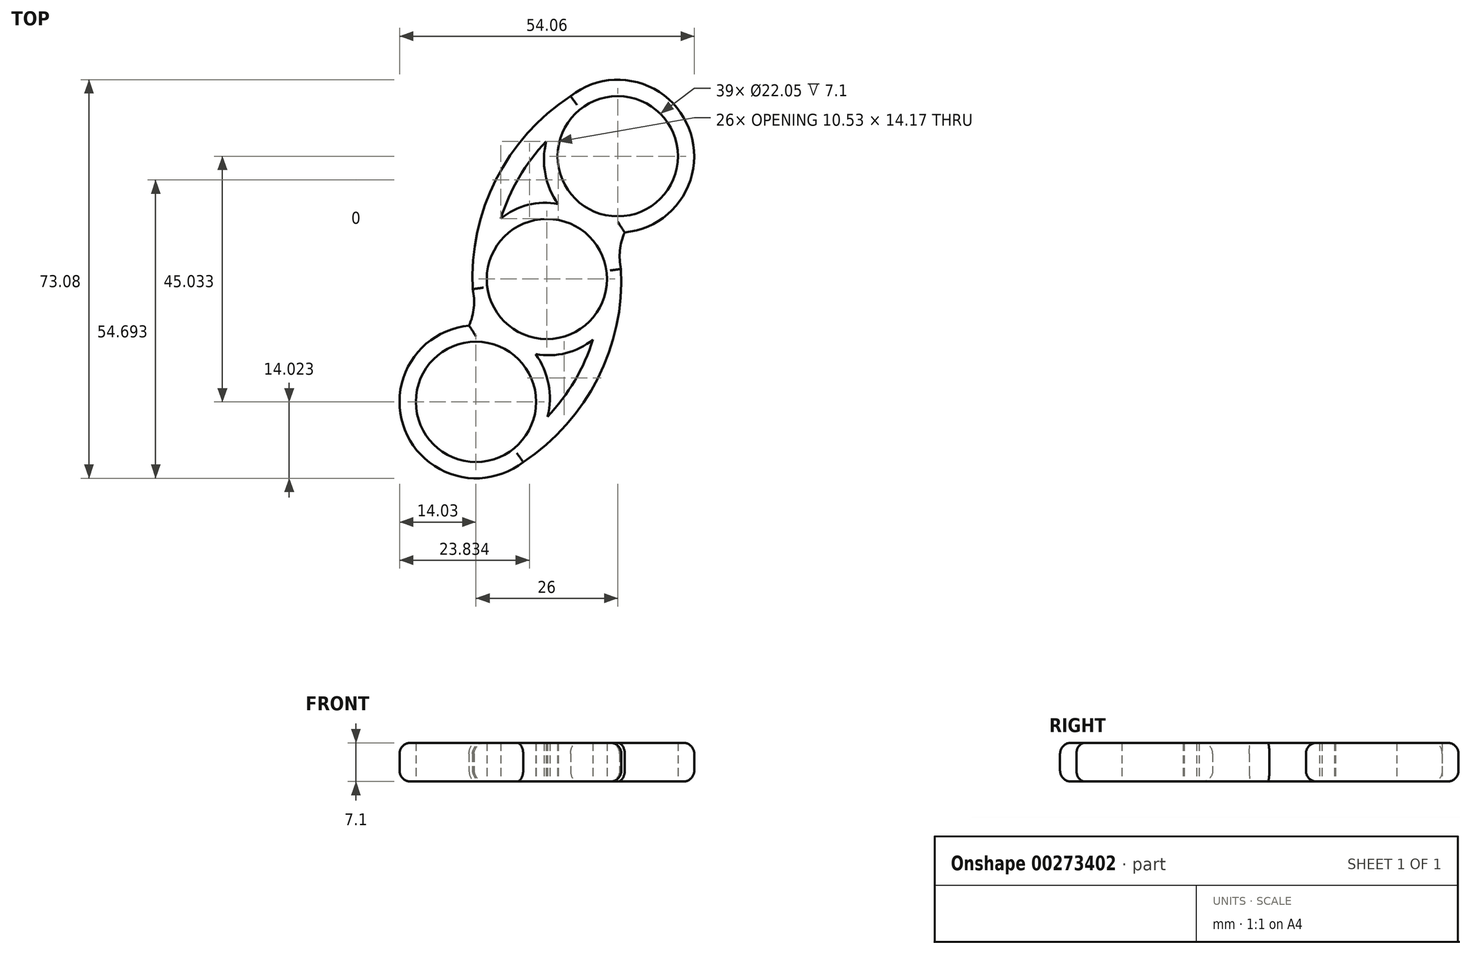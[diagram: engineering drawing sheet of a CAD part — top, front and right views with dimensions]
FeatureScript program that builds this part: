
annotation { "Feature Type Name" : "Feature", "Feature Type Description" : "" }
export const myFeature = defineFeature(function(context is Context, id is Id, definition is map)
    precondition{}
    {
        {
            var Q0;
            Q0=qCreatedBy(makeId("Top.planeOp"),FACE);
            var sketch = newSketch(context, id + "F0", { "sketchPlane" : qUnion([Q0])});
            skCircle(sketch, "E0", {"center": v(0, 0) * mm, "radius": 11.03 * mm});
            skCircle(sketch, "E1", {"center": v(13, 22.52) * mm, "radius": 11.03 * mm});
            skLineSegment(sketch, "E2", {"start": v(0, 0) * mm, "end": v(13, 22.52) * mm, "construction": true});
            skArc(sketch, "E3", {"start": v(14.28, 8.55) * mm, "mid": v(26.03, 27.7) * mm, "end": v(4.35, 33.55) * mm});
            skLineSegment(sketch, "E4", {"start": v(13, 22.52) * mm, "end": v(0.85, 29.53) * mm, "construction": true});
            skPoint(sketch, "E5.visualSharp", {"position": v(5.99, 10.37) * mm});
            skLineSegment(sketch, "E6", {"start": v(13, 22.52) * mm, "end": v(25.15, 15.5) * mm, "construction": true});
            skCircle(sketch, "E7", {"center": v(0, 0) * mm, "radius": 11.36 * mm, "construction": true});
            skPoint(sketch, "E8.center", {"position": v(-0.23, 0.06) * mm});
            skPoint(sketch, "E9.orphan", {"position": v(-5.27, 14.87) * mm});
            skPoint(sketch, "E10.orphan", {"position": v(7.2, 12.48) * mm});
            skPoint(sketch, "E11.1.5", {"position": v(0.06, -0.23) * mm});
            skPoint(sketch, "E11.1.6", {"position": v(-10.25, -11) * mm});
            skPoint(sketch, "E11.2.5", {"position": v(0.17, 0.17) * mm});
            skCircle(sketch, "E12.1.0", {"center": v(-13, -22.52) * mm, "radius": 11.03 * mm});
            skLineSegment(sketch, "E12.1.1", {"start": v(-13, -22.52) * mm, "end": v(-0.85, -29.53) * mm, "construction": true});
            skArc(sketch, "E12.1.2", {"start": v(-14.28, -8.55) * mm, "mid": v(-26.03, -27.7) * mm, "end": v(-4.35, -33.55) * mm});
            skLineSegment(sketch, "E12.1.3", {"start": v(-13, -22.52) * mm, "end": v(-25.15, -15.5) * mm, "construction": true});
            skArc(sketch, "E13", {"start": v(-4.35, -33.55) * mm, "mid": v(9.34, -18.24) * mm, "end": v(13.6, 1.84) * mm});
            skArc(sketch, "E14", {"start": v(14.28, 8.55) * mm, "mid": v(13.4, 5.25) * mm, "end": v(13.6, 1.84) * mm});
            skArc(sketch, "E15.1.0", {"start": v(-14.28, -8.55) * mm, "mid": v(-13.4, -5.25) * mm, "end": v(-13.6, -1.84) * mm});
            skArc(sketch, "E15.1.1", {"start": v(4.35, 33.55) * mm, "mid": v(-9.34, 18.24) * mm, "end": v(-13.6, -1.84) * mm});
            skArc(sketch, "E16", {"start": v(2.07, 13.75) * mm, "mid": v(-3.5, 13.58) * mm, "end": v(-8.46, 11.07) * mm});
            skArc(sketch, "E17", {"start": v(-0.13, 25.24) * mm, "mid": v(-0.3, 19.25) * mm, "end": v(2.07, 13.75) * mm});
            skPoint(sketch, "E18.orphan", {"position": v(1.15, 27.06) * mm});
            skPoint(sketch, "E19.orphan", {"position": v(3.03, 13.53) * mm});
            skArc(sketch, "E20.0", {"start": v(-0.13, 25.24) * mm, "mid": v(-5.1, 18.63) * mm, "end": v(-8.46, 11.07) * mm});
            skPoint(sketch, "E21.orphan", {"position": v(-9.03, 10.57) * mm});
            skPoint(sketch, "E22.orphan", {"position": v(0.1, 26.05) * mm});
            skArc(sketch, "E23.1.0", {"start": v(0.13, -25.24) * mm, "mid": v(5.1, -18.63) * mm, "end": v(8.46, -11.07) * mm});
            skArc(sketch, "E23.1.1", {"start": v(0.13, -25.24) * mm, "mid": v(0.3, -19.25) * mm, "end": v(-2.07, -13.75) * mm});
            skArc(sketch, "E23.1.2", {"start": v(-2.07, -13.75) * mm, "mid": v(3.5, -13.58) * mm, "end": v(8.46, -11.07) * mm});
            skSolve(sketch);
        }
        {
            var Q0;
            Q0=makeQuery(id+"F0.imprint","IMPRINT",FACE,{"disambiguationData":[TD([[makeQuery(id+"F0.imprint","IMPRINT",EDGE,{"derivedFrom":sQuery(id+"F0.wireOp",EDGE,"ea44153e-c5e4-4200-878d-53ebf284e07f.1.0")}),-1.0]])]});
            var Q1;
            Q1=makeQuery(id+"F0.imprint","IMPRINT",FACE,{"disambiguationData":[TD([[makeQuery(id+"F0.imprint","IMPRINT",EDGE,{"derivedFrom":sQuery(id+"F0.wireOp",EDGE,"E0")}),-1.0]])]});
            var Q2;
            Q2=makeQuery(id+"F0.imprint","IMPRINT",FACE,{"disambiguationData":[TD([[makeQuery(id+"F0.imprint","IMPRINT",EDGE,{"derivedFrom":sQuery(id+"F0.wireOp",EDGE,"E1")}),-1.0]])]});
            var Q3;
            {var subQ0=sQuery(id+"F0.wireOp",EDGE,"zqQpl2xC-KShR-byGl-JfGq-b1LpVGurQPJH");Q3=makeQuery(id+"F0.imprint","IMPRINT",FACE,{"disambiguationData":[TD([[makeQuery(id+"F0.imprint","IMPRINT",EDGE,{"derivedFrom":subQ0}),-1.0]])]});}
            extrude(context, id + "F1", {"entities" : qUnion([Q0, Q1, Q2, Q3]), "depth" : 7.1 * mm});
        }
        {
            var Q0;
            Q0=makeQuery(id+"F1.opExtrude","CAP_EDGE",EDGE,{"disambiguationData":[OSD([sQuery(id+"F0.wireOp",EDGE,"E15.1.1")])],"isStart":false});
            var Q1;
            Q1=makeQuery(id+"F1.opExtrude","CAP_EDGE",EDGE,{"disambiguationData":[OSD([sQuery(id+"F0.wireOp",EDGE,"E15.1.0")])],"isStart":false});
            var Q2;
            Q2=makeQuery(id+"F1.opExtrude","CAP_EDGE",EDGE,{"disambiguationData":[OSD([sQuery(id+"F0.wireOp",EDGE,"E12.1.2")])],"isStart":false});
            var Q3;
            Q3=makeQuery(id+"F1.opExtrude","CAP_EDGE",EDGE,{"disambiguationData":[OSD([sQuery(id+"F0.wireOp",EDGE,"E13")])],"isStart":false});
            var Q4;
            Q4=makeQuery(id+"F1.opExtrude","CAP_EDGE",EDGE,{"disambiguationData":[OSD([sQuery(id+"F0.wireOp",EDGE,"E14")])],"isStart":false});
            var Q5;
            Q5=makeQuery(id+"F1.opExtrude","CAP_EDGE",EDGE,{"disambiguationData":[OSD([sQuery(id+"F0.wireOp",EDGE,"E3")])],"isStart":false});
            var Q6;
            Q6=makeQuery(id+"F1.opExtrude","CAP_EDGE",EDGE,{"disambiguationData":[OSD([sQuery(id+"F0.wireOp",EDGE,"E12.1.2")])],"isStart":true});
            var Q7;
            Q7=makeQuery(id+"F1.opExtrude","CAP_EDGE",EDGE,{"disambiguationData":[OSD([sQuery(id+"F0.wireOp",EDGE,"E15.1.0")])],"isStart":true});
            var Q8;
            Q8=makeQuery(id+"F1.opExtrude","CAP_EDGE",EDGE,{"disambiguationData":[OSD([sQuery(id+"F0.wireOp",EDGE,"E15.1.1")])],"isStart":true});
            var Q9;
            Q9=makeQuery(id+"F1.opExtrude","CAP_EDGE",EDGE,{"disambiguationData":[OSD([sQuery(id+"F0.wireOp",EDGE,"E13")])],"isStart":true});
            var Q10;
            Q10=makeQuery(id+"F1.opExtrude","CAP_EDGE",EDGE,{"disambiguationData":[OSD([sQuery(id+"F0.wireOp",EDGE,"E14")])],"isStart":true});
            var Q11;
            Q11=makeQuery(id+"F1.opExtrude","CAP_EDGE",EDGE,{"disambiguationData":[OSD([sQuery(id+"F0.wireOp",EDGE,"E3")])],"isStart":true});
            fillet(context, id + "F2", {"entities" : qUnion([Q0, Q1, Q2, Q3, Q4, Q5, Q6, Q7, Q8, Q9, Q10, Q11]), "radius" : 2 * mm, "allowEdgeOverflow" : false});
        }
    });
